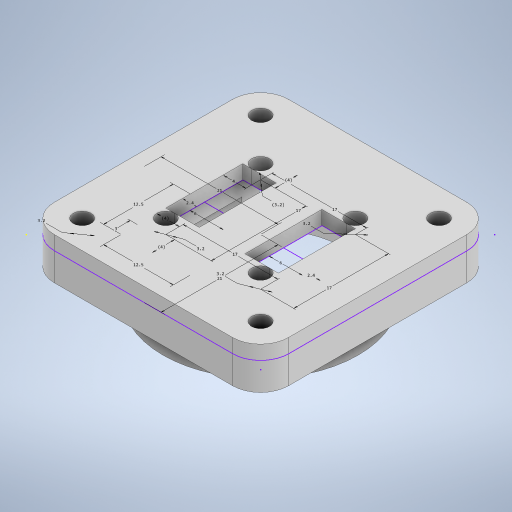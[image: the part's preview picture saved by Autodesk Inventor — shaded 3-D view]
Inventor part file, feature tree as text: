
AUTODESK INVENTOR PART (.ipt)
format: ipt  version: 2024 (Build 280153000, 153)  size: 349,696 bytes
history: native  units: mm
features: extrude x3, sketch x2, other x1
ambient origin geometry x8: Origin, YZ Plane, XZ Plane, XY Plane, X Axis, Y Axis, Z Axis, Center Point
bodies: Body1 (feature_tree)
feature tree (6):
  other  "ソリッド1"
  sketch  "スケッチ1"
  extrude  "押し出し2"  Depth=21.0mm
  extrude  "押し出し3"  Depth=21.0mm
  extrude  "押し出し4"  Depth=3.2mm
  sketch  "スケッチ2"
